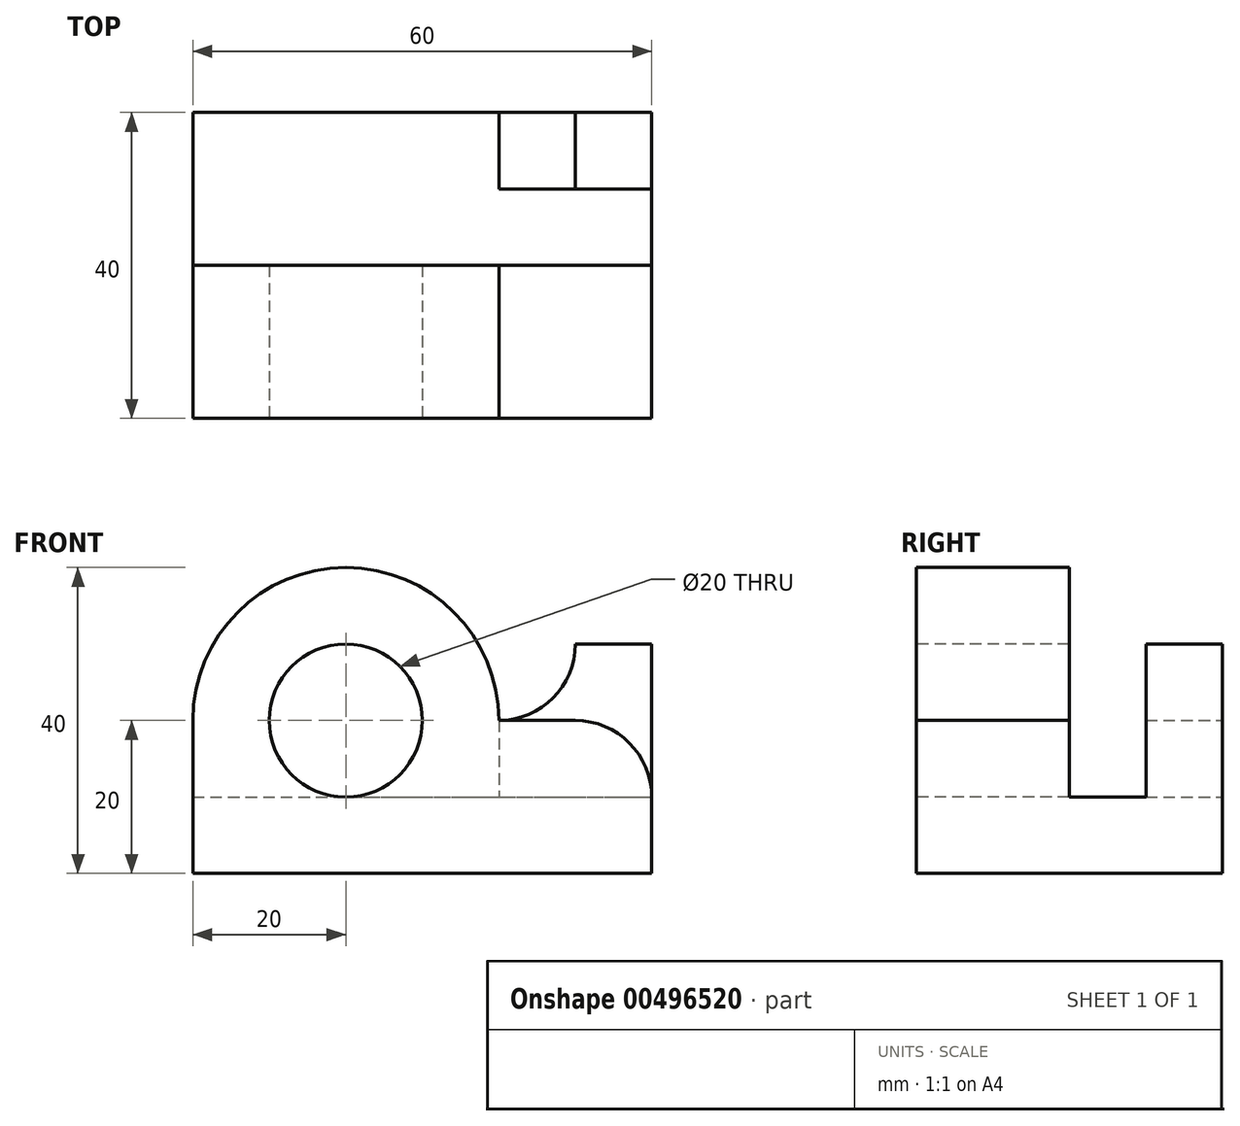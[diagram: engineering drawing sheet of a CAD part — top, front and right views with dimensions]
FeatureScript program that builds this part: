
annotation { "Feature Type Name" : "Feature", "Feature Type Description" : "" }
export const myFeature = defineFeature(function(context is Context, id is Id, definition is map)
    precondition{}
    {
        {
            var Q0;
            Q0=qCreatedBy(makeId("Top.planeOp"),FACE);
            var sketch = newSketch(context, id + "F0", { "sketchPlane" : qUnion([Q0])});
            skLineSegment(sketch, "E0", {"start": v(0, 0) * mm, "end": v(0, 40) * mm});
            skLineSegment(sketch, "E1", {"start": v(0, 40) * mm, "end": v(60, 40) * mm});
            skLineSegment(sketch, "E2", {"start": v(60, 40) * mm, "end": v(60, 0) * mm});
            skLineSegment(sketch, "E3", {"start": v(60, 0) * mm, "end": v(0, 0) * mm});
            skSolve(sketch);
        }
        {
            var Q0;
            Q0=qSketchRegion(id+"F0",true);
            extrude(context, id + "F1", {"entities" : qUnion([Q0]), "depth" : 10 * mm});
        }
        {
            var Q0;
            Q0=qCreatedBy(makeId("Front.planeOp"),FACE);
            var sketch = newSketch(context, id + "F2", { "sketchPlane" : qUnion([Q0])});
            skPoint(sketch, "E4", {"position": v(20, 20) * mm});
            skArc(sketch, "E5", {"start": v(40, 20) * mm, "mid": v(20, 40) * mm, "end": v(0, 20) * mm});
            skLineSegment(sketch, "E6", {"start": v(40, 20) * mm, "end": v(50, 20) * mm});
            skLineSegment(sketch, "E7", {"start": v(60, 10) * mm, "end": v(60, 10) * mm});
            skLineSegment(sketch, "E8", {"start": v(0, 10) * mm, "end": v(0, 20) * mm});
            skLineSegment(sketch, "E9", {"start": v(0, 10) * mm, "end": v(60, 10) * mm});
            skPoint(sketch, "E10.visualSharp", {"position": v(60, 20) * mm});
            skArc(sketch, "E10.filletArc", {"start": v(60, 10) * mm, "mid": v(57.07, 17.07) * mm, "end": v(50, 20) * mm});
            skSolve(sketch);
        }
        {
            var Q0;
            Q0=qSketchRegion(id+"F2",true);
            extrude(context, id + "F3", {"entities" : qUnion([Q0]), "operationType" : NewBodyOperationType.ADD, "oppositeDirection" : true, "depth" : 20 * mm});
        }
        {
            var Q0;
            Q0=makeQuery(id+"F3.boolean.opBoolean","MERGE",FACE,{"derivedFrom":[makeQuery(id+"F1.opExtrude","SWEPT_FACE",FACE,{"disambiguationData":[OSD([sQuery(id+"F0.wireOp",EDGE,"E3")])]}),makeQuery(id+"F3.opExtrude","CAP_FACE",FACE,{"disambiguationData":[OSD([sQuery(id+"F2.wireOp",EDGE,"E5"),sQuery(id+"F2.wireOp",EDGE,"E6"),sQuery(id+"F2.wireOp",EDGE,"E8"),sQuery(id+"F2.wireOp",EDGE,"E9"),sQuery(id+"F2.wireOp",EDGE,"E10.filletArc")])],"isStart":true})]});
            var sketch = newSketch(context, id + "F4", { "sketchPlane" : qUnion([Q0])});
            skLineSegment(sketch, "E11", {"start": v(60, 10) * mm, "end": v(0, 10) * mm});
            skLineSegment(sketch, "E12", {"start": v(0, 10) * mm, "end": v(0, 20) * mm});
            skCircle(sketch, "E13", {"center": v(20, 20) * mm, "radius": 10 * mm});
            skSolve(sketch);
        }
        {
            var Q0;
            Q0=makeQuery(id+"F4.imprint","IMPRINT",FACE,{"disambiguationData":[TD([[makeQuery(id+"F4.imprint","IMPRINT",EDGE,{"derivedFrom":sQuery(id+"F4.wireOp",EDGE,"E13")}),1.0]])]});
            extrude(context, id + "F5", {"entities" : qUnion([Q0]), "operationType" : NewBodyOperationType.REMOVE, "oppositeDirection" : true, "depth" : 25 * mm});
        }
        {
            var Q0;
            Q0=makeQuery(id+"F1.opExtrude","SWEPT_FACE",FACE,{"disambiguationData":[OSD([sQuery(id+"F0.wireOp",EDGE,"E1")])]});
            var sketch = newSketch(context, id + "F6", { "sketchPlane" : qUnion([Q0])});
            skLineSegment(sketch, "E14", {"start": v(-60, 10) * mm, "end": v(-60, 30) * mm});
            skLineSegment(sketch, "E15", {"start": v(-60, 30) * mm, "end": v(-50, 30) * mm});
            skLineSegment(sketch, "E16", {"start": v(-50, 30) * mm, "end": v(-50, 20) * mm});
            skLineSegment(sketch, "E17", {"start": v(-50, 20) * mm, "end": v(-40, 20) * mm});
            skLineSegment(sketch, "E18", {"start": v(-40, 20) * mm, "end": v(-40, 10) * mm});
            skLineSegment(sketch, "E19", {"start": v(-40, 10) * mm, "end": v(-60, 10) * mm});
            skSolve(sketch);
        }
        {
            var Q0;
            Q0 = qSketchRegion(id + "F6", true);
            extrude(context, id + "F7", {"entities" : qUnion([Q0]), "operationType" : NewBodyOperationType.ADD, "depth" : -10 * mm, "offsetDistance" : 25 * mm});
        }
        {
            var Q0;
            Q0=makeQuery(id+"F7.opExtrude","SWEPT_EDGE",EDGE,{"disambiguationData":[OSD([sQuery(id+"F6.wireOp",EDGE,"E16"),sQuery(id+"F6.wireOp",EDGE,"E17")])]});
            fillet(context, id + "F8", {"entities" : qUnion([Q0]), "radius" : 10 * mm, "tangentPropagation" : true, "allowEdgeOverflow" : false});
        }
    });
